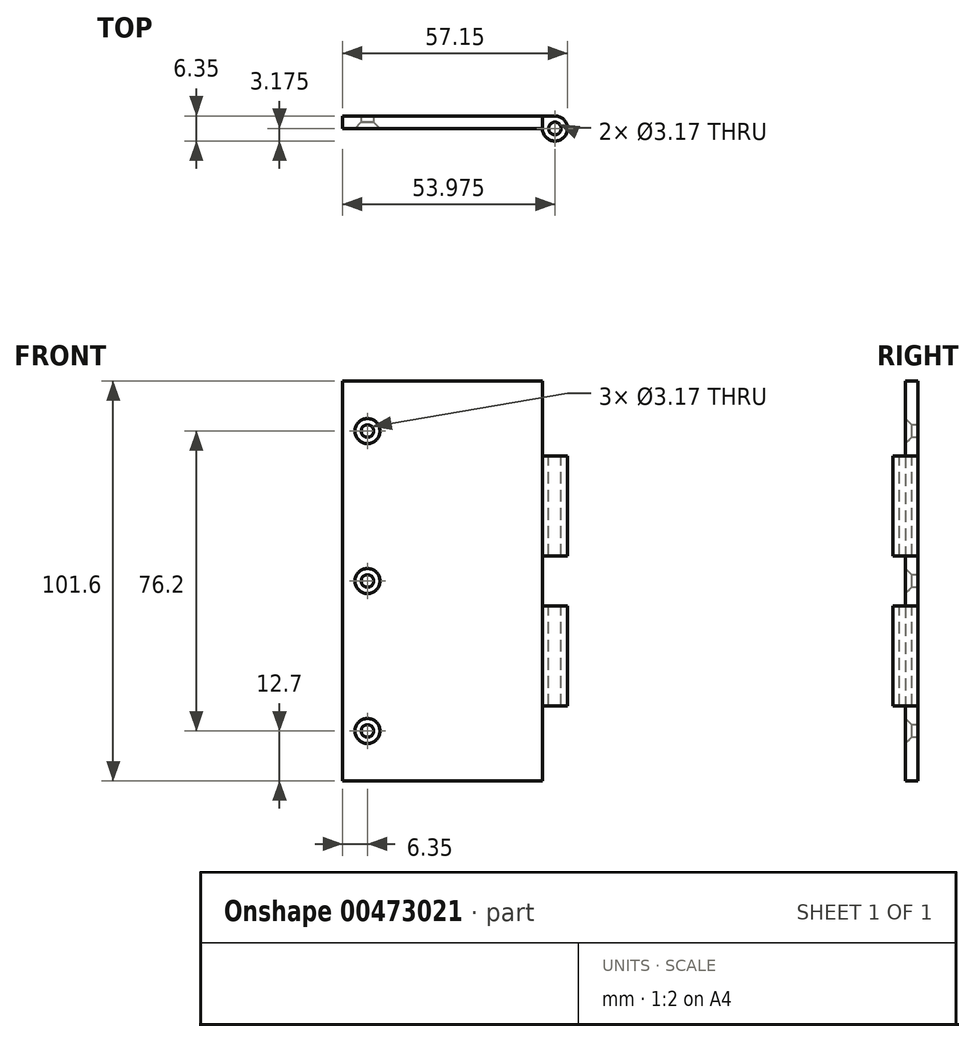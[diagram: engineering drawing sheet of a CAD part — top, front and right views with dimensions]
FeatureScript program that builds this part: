
annotation { "Feature Type Name" : "Feature", "Feature Type Description" : "" }
export const myFeature = defineFeature(function(context is Context, id is Id, definition is map)
    precondition{}
    {
        {
            var Q0;
            Q0=qCreatedBy(makeId("Front.planeOp"),FACE);
            var sketch = newSketch(context, id + "F0", { "sketchPlane" : qUnion([Q0])});
            skLineSegment(sketch, "E0.bottom", {"start": v(25.4, 50.8) * mm, "end": v(-25.4, 50.8) * mm});
            skLineSegment(sketch, "E0.top", {"start": v(25.4, -50.8) * mm, "end": v(-25.4, -50.8) * mm});
            skLineSegment(sketch, "E0.left", {"start": v(25.4, 50.8) * mm, "end": v(25.4, -50.8) * mm});
            skLineSegment(sketch, "E0.right", {"start": v(-25.4, 50.8) * mm, "end": v(-25.4, -50.8) * mm});
            skPoint(sketch, "E0.middle", {"position": v(0, 0) * mm});
            skSolve(sketch);
        }
        {
            var Q0;
            Q0=makeQuery(id+"F0.imprint","IMPRINT",FACE,{"disambiguationData":[TD([[makeQuery(id+"F0.imprint","IMPRINT",EDGE,{"derivedFrom":sQuery(id+"F0.wireOp",EDGE,"E0.bottom")}),1.0]])]});
            extrude(context, id + "F1", {"entities" : qUnion([Q0]), "depth" : 3.17 * mm});
        }
        {
            var Q0;
            Q0=makeQuery(id+"F1.opExtrude","SWEPT_FACE",FACE,{"disambiguationData":[OSD([sQuery(id+"F0.wireOp",EDGE,"E0.left")])]});
            var sketch = newSketch(context, id + "F2", { "sketchPlane" : qUnion([Q0])});
            skLineSegment(sketch, "E1.top", {"start": v(0, 31.75) * mm, "end": v(-6.35, 31.75) * mm});
            skLineSegment(sketch, "E2.bottom", {"start": v(0, 6.35) * mm, "end": v(-6.35, 6.35) * mm});
            skLineSegment(sketch, "E2.top", {"start": v(0, -6.35) * mm, "end": v(-6.35, -6.35) * mm});
            skLineSegment(sketch, "E3.top", {"start": v(0, -31.75) * mm, "end": v(-6.35, -31.75) * mm});
            skLineSegment(sketch, "E4.left", {"start": v(0, 31.75) * mm, "end": v(0, 6.35) * mm});
            skLineSegment(sketch, "E4.right", {"start": v(-6.35, 31.75) * mm, "end": v(-6.35, 6.35) * mm});
            skLineSegment(sketch, "E5.left", {"start": v(0, -6.35) * mm, "end": v(0, -31.75) * mm});
            skLineSegment(sketch, "E5.right", {"start": v(-6.35, -6.35) * mm, "end": v(-6.35, -31.75) * mm});
            skSolve(sketch);
        }
        {
            var Q0;
            Q0 = qSketchRegion(id + "F2", true);
            extrude(context, id + "F3", {"entities" : qUnion([Q0]), "operationType" : NewBodyOperationType.ADD, "depth" : 6.35 * mm});
        }
        {
            var Q0;
            Q0=makeQuery(id+"F3.opExtrude","SWEPT_FACE",FACE,{"disambiguationData":[OSD([sQuery(id+"F2.wireOp",EDGE,"E1.top")])]});
            var sketch = newSketch(context, id + "F4", { "sketchPlane" : qUnion([Q0])});
            skCircle(sketch, "E6", {"center": v(28.57, -3.17) * mm, "radius": 3.17 * mm});
            skPoint(sketch, "E6.centerSnap0", {"position": v(31.75, -3.17) * mm});
            skPoint(sketch, "E6.centerSnap1", {"position": v(28.57, -6.35) * mm});
            skSolve(sketch);
        }
        {
            var Q0;
            {var subQ1=sQuery(id+"F2.wireOp",EDGE,"E1.top");var subQ3=makeQuery(id+"F3.opExtrude","CAP_EDGE",EDGE,{"disambiguationData":[OSD([subQ1])],"isStart":true});var subQ4=sQuery(id+"F2.wireOp",EDGE,"E4.right");var subQ5=makeQuery(id+"F3.boolean.opBoolean","SPLIT",EDGE,{"disambiguationData":[topologyDisambiguationEdgeConnected([makeQuery(id+"F3.opExtrude","CAP_FACE",FACE,{"disambiguationData":[OSD([subQ1,sQuery(id+"F2.wireOp",EDGE,"E2.bottom"),sQuery(id+"F2.wireOp",EDGE,"E4.left"),subQ4])],"isStart":true})])],"derivedFrom":subQ3});Q0=makeQuery(id+"F4.imprint","IMPRINT",FACE,{"disambiguationData":[TD([[makeQuery(id+"F4.imprint","IMPRINT",EDGE,{"derivedFrom":subQ5}),1.0]])]});}
            var Q1;
            {var subQ0=sQuery(id+"F4.wireOp",EDGE,"E6");var subQ1=sQuery(id+"F2.wireOp",EDGE,"E1.top");var subQ2=makeQuery(id+"F3.opExtrude","CAP_EDGE",EDGE,{"disambiguationData":[OSD([subQ1])],"isStart":false});var subQ3=makeQuery(id+"F4.imprint","INTERSECT",VERTEX,{"derivedFrom":[subQ2,subQ0]});Q1=makeQuery(id+"F4.imprint","IMPRINT",FACE,{"disambiguationData":[TD([[makeQuery(id+"F4.imprint","IMPRINT",EDGE,{"disambiguationData":[TD([[subQ3,1.0]])],"derivedFrom":subQ0}),-1.0]])]});}
            var Q2;
            {var subQ0=sQuery(id+"F4.wireOp",EDGE,"E6");var subQ1=sQuery(id+"F2.wireOp",EDGE,"E1.top");var subQ4=makeQuery(id+"F3.opExtrude","CAP_EDGE",EDGE,{"disambiguationData":[OSD([subQ1])],"isStart":false});var subQ5=makeQuery(id+"F4.imprint","INTERSECT",VERTEX,{"derivedFrom":[subQ4,subQ0]});Q2=makeQuery(id+"F4.imprint","IMPRINT",FACE,{"disambiguationData":[TD([[makeQuery(id+"F4.imprint","IMPRINT",EDGE,{"disambiguationData":[TD([[subQ5,-1.0]])],"derivedFrom":subQ0}),-1.0]])]});}
            extrude(context, id + "F5", {"entities" : qUnion([Q0, Q1, Q2]), "operationType" : NewBodyOperationType.REMOVE, "endBound" : BoundingType.THROUGH_ALL, "oppositeDirection" : true, "depth" : 25.4 * mm});
        }
        {
            var Q0;
            Q0=makeQuery(id+"F3.opExtrude","SWEPT_FACE",FACE,{"disambiguationData":[OSD([sQuery(id+"F2.wireOp",EDGE,"E1.top")])]});
            var sketch = newSketch(context, id + "F6", { "sketchPlane" : qUnion([Q0])});
            skCircle(sketch, "E7", {"center": v(28.58, -3.17) * mm, "radius": 1.59 * mm});
            skSolve(sketch);
        }
        {
            var Q0;
            Q0=makeQuery(id+"F6.imprint","IMPRINT",FACE,{"disambiguationData":[TD([[makeQuery(id+"F6.imprint","IMPRINT",EDGE,{"derivedFrom":sQuery(id+"F6.wireOp",EDGE,"E7")}),1.0]])]});
            extrude(context, id + "F7", {"entities" : qUnion([Q0]), "operationType" : NewBodyOperationType.REMOVE, "endBound" : BoundingType.THROUGH_ALL, "oppositeDirection" : true, "depth" : 25.4 * mm});
        }
        {
            var Q0;
            Q0=makeQuery(id+"F1.opExtrude","CAP_FACE",FACE,{"disambiguationData":[OSD([sQuery(id+"F0.wireOp",EDGE,"E0.bottom"),sQuery(id+"F0.wireOp",EDGE,"E0.top"),sQuery(id+"F0.wireOp",EDGE,"E0.left"),sQuery(id+"F0.wireOp",EDGE,"E0.right")])],"isStart":false});
            var sketch = newSketch(context, id + "F8", { "sketchPlane" : qUnion([Q0])});
            skLineSegment(sketch, "E8", {"start": v(-25.4, 0) * mm, "end": v(-19.05, 0) * mm});
            skPoint(sketch, "E8.endSnap0", {"position": v(-25.4, 0) * mm});
            skLineSegment(sketch, "E9.0", {"start": v(-25.4, 38.1) * mm, "end": v(-19.05, 38.1) * mm});
            skLineSegment(sketch, "E10.0", {"start": v(-25.4, -38.1) * mm, "end": v(-19.05, -38.1) * mm});
            skSolve(sketch);
        }
        {
            var Q0;
            Q0=sQuery(id+"F8.wireOp",VERTEX,"E9.0.end");
            var Q1;
            Q1=sQuery(id+"F8.wireOp",VERTEX,"E8.end");
            var Q2;
            Q2=sQuery(id+"F8.wireOp",VERTEX,"E10.0.end");
            var Q3;
            Q3=makeQuery(id+"F1.opExtrude","SWEPT_BODY",BODY,{"disambiguationData":[OSD([sQuery(id+"F0.wireOp",EDGE,"E0.bottom"),sQuery(id+"F0.wireOp",EDGE,"E0.top"),sQuery(id+"F0.wireOp",EDGE,"E0.left"),sQuery(id+"F0.wireOp",EDGE,"E0.right")])]});
            hole(context, id + "F9", {"style" : HoleStyle.C_SINK, "endStyle" : HoleEndStyle.THROUGH, "holeDiameter" : 3.17 * mm, "cSinkDiameter" : 6.35 * mm, "cSinkAngle" : 90 * degree, "isTappedThrough" : true, "tappedDepth" : 12.7 * mm, "tapClearance" : 3, "locations" : qUnion([Q0, Q1, Q2]), "scope" : qUnion([Q3])});
        }
    });
